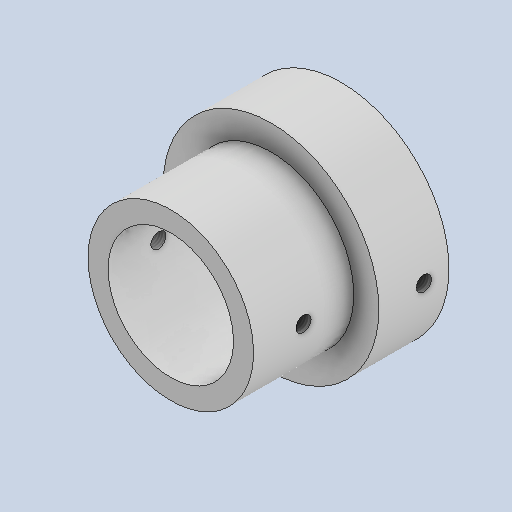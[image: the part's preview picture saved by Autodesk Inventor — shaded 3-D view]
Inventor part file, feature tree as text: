
AUTODESK INVENTOR PART (.ipt)
format: ipt  version: 2023 (Build 270158000, 158)  size: 290,304 bytes
history: native  units: mm
features: thread x2, sketch x2, other x1, revolve x1, extrude x1
ambient origin geometry x8: Origin, YZ Plane, XZ Plane, XY Plane, X Axis, Y Axis, Z Axis, Center Point
bodies: Body1 (feature_tree)
feature tree (7):
  other  "Твердое тело1"
  revolve  "Вращение1"
  extrude  "Выдавливание1"  Depth=12.5mm
  thread  "Резьба1"
  thread  "Резьба2"
  sketch  "Эскиз1"
  sketch  "Эскиз2"
